# Revit family: 205_SIL-50-_-1500
name_source: partatom
category: Duct Accessories
units: mm (PartAtom-declared; Revit-internal decimal feet)

## family parameters
Always vertical = Yes
Cut with Voids When Loaded = No
Part Type = Breaks Into
Round Connector Dimension = Use Diameter
Shared = No
Work Plane-Based = No

## types (6) — shared parameters
Description = CIRCULAR SILENCER
L2D = 1500 mm  [stored 4.92126 ft]
LL = 750 mm  [stored 2.46063 ft]
Manufacturer = Alnor
QmdConnectorList = 201;D;202;D
URL = http://www.ventilation-alnor.co.uk
magiPartTypeId = 205
magiProductFamilyId = SIL-50-*-1500

## per-type parameters (varying)
| type | CD1 | CD2 | D | H2D | L1 | L2 | R | SW1 | W2D |
| SIL-50-250-1500 | 178 mm | 179 mm | 250 mm | 350 mm | 36 mm  [stored 0.11811 ft] | 1428 mm  [stored 4.68504 ft] | 125 mm  [stored 0.410105 ft] | No | 350 mm |
| SIL-50-500-1500 | 300 mm | 301 mm | 500 mm | 600 mm | 4 mm  [stored 0.0131234 ft] | 1492 mm | 250 mm  [stored 0.82021 ft] | Yes | 600 mm |
| SIL-50-450-1500 | 280 mm | 281 mm | 450 mm | 550 mm | 4 mm  [stored 0.0131234 ft] | 1492 mm | 225 mm | Yes | 550 mm |
| SIL-50-400-1500 | 250 mm  [stored 0.82021 ft] | 251 mm | 400 mm | 500 mm | 4 mm  [stored 0.0131234 ft] | 1492 mm | 200 mm | Yes | 500 mm |
| SIL-50-315-1500 | 200 mm | 201 mm | 315 mm | 415 mm | 4 mm  [stored 0.0131234 ft] | 1492 mm | 158 mm | Yes | 415 mm |
| SIL-50-300-1500 | 200 mm | 201 mm | 300 mm | 400 mm | 4 mm  [stored 0.0131234 ft] | 1492 mm | 150 mm | Yes | 400 mm |

note: column(s) folded — value = type name in every type: MC Product Code, magiProductId

note: [stored X ft] marks values corroborated as IEEE doubles in the binary element streams (Revit-internal decimal feet)

## geometry (parser evidence)
native form markers: Blend x4, Sweep x1
no freeform markers — native parametric forms only
